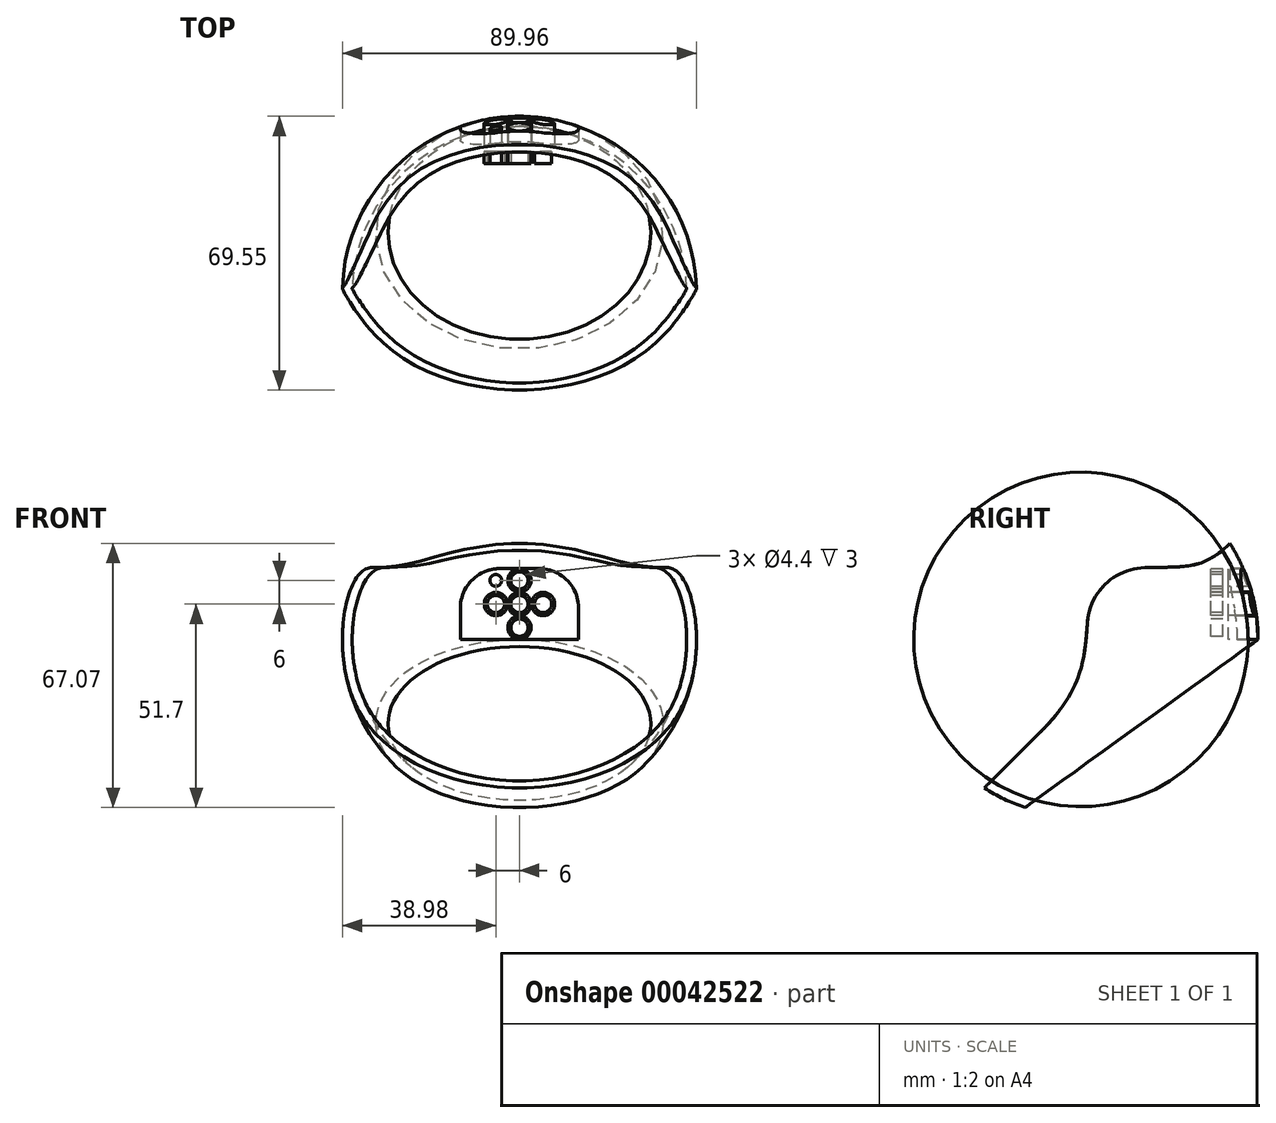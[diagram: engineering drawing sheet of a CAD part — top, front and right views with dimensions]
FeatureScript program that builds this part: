
annotation { "Feature Type Name" : "Feature", "Feature Type Description" : "" }
export const myFeature = defineFeature(function(context is Context, id is Id, definition is map)
    precondition{}
    {
        {
            var Q0;
            Q0=qCreatedBy(makeId("Right.planeOp"),FACE);
            var sketch = newSketch(context, id + "F0", { "sketchPlane" : qUnion([Q0])});
            skArc(sketch, "E0", {"start": v(40, 0) * mm, "mid": v(38.33, 11.42) * mm, "end": v(33.48, 21.9) * mm});
            skLineSegment(sketch, "E1", {"start": v(0, -40) * mm, "end": v(0, 40) * mm, "construction": true});
            skLineSegment(sketch, "E2", {"start": v(-40, 0) * mm, "end": v(40, 0) * mm, "construction": true});
            skPoint(sketch, "E3", {"position": v(33.48, 21.9) * mm});
            skPoint(sketch, "E4", {"position": v(-21.9, -33.48) * mm});
            skLineSegment(sketch, "E5", {"start": v(-21.9, -33.48) * mm, "end": v(33.48, 21.9) * mm, "construction": true});
            skPoint(sketch, "E6", {"position": v(12.26, 0.68) * mm});
            skPoint(sketch, "E7", {"position": v(-7.75, -19.33) * mm});
            skFitSpline(sketch, "E8", {"points": [v(-7.75, -19.33) * mm, v(4.22, 8.7) * mm], "startDerivative": vector(26.03, 26.03) * mm, "endDerivative": vector(-1.06, 47.13) * mm});
            skFitSpline(sketch, "E9", {"points": [v(33.48, 21.9) * mm, v(12.36, 15.68) * mm], "startDerivative": vector(-15.28, -15.28) * mm, "endDerivative": vector(-38.84, 5.85) * mm});
            skArc(sketch, "E10.trimOffspring", {"start": v(20.07, 15.1) * mm, "mid": v(11.15, 14.38) * mm, "end": v(4.22, 8.7) * mm});
            skLineSegment(sketch, "E11", {"start": v(33.48, 21.9) * mm, "end": v(40, 21.9) * mm});
            skLineSegment(sketch, "E12", {"start": v(40, 0) * mm, "end": v(40, 21.9) * mm});
            skCircle(sketch, "E13", {"center": v(0, 0) * mm, "radius": 40 * mm, "construction": true});
            skPoint(sketch, "E14", {"position": v(0, -32.17) * mm});
            skPoint(sketch, "E15", {"position": v(40, 0) * mm});
            skLineSegment(sketch, "E16", {"start": v(-21.9, -33.48) * mm, "end": v(-14.82, -40.55) * mm});
            skLineSegment(sketch, "E17", {"start": v(-14.82, -40.55) * mm, "end": v(40, 0) * mm});
            skLineSegment(sketch, "E18", {"start": v(-14.82, -40.55) * mm, "end": v(-21.9, -40.55) * mm});
            skLineSegment(sketch, "E19", {"start": v(-21.9, -33.48) * mm, "end": v(-21.9, -40.55) * mm});
            skLineSegment(sketch, "E20", {"start": v(-21.9, -33.48) * mm, "end": v(-7.75, -19.33) * mm});
            skPoint(sketch, "E21", {"position": v(-40, 0) * mm});
            skSolve(sketch);
        }
        {
            var Q0;
            Q0=qCreatedBy(makeId("Top.planeOp"),FACE);
            var sketch = newSketch(context, id + "F1", { "sketchPlane" : qUnion([Q0])});
            skArc(sketch, "E22", {"start": v(42.5, 0) * mm, "mid": v(0, 42.5) * mm, "end": v(-42.5, 0) * mm});
            skArc(sketch, "E23", {"start": v(45, 0) * mm, "mid": v(0, 45) * mm, "end": v(-45, 0) * mm});
            skLineSegment(sketch, "E24", {"start": v(16.73, 41.77) * mm, "end": v(7.83, 41.77) * mm});
            skLineSegment(sketch, "E25.trimOffspring", {"start": v(-7.83, 41.77) * mm, "end": v(-16.73, 41.77) * mm});
            skLineSegment(sketch, "E26", {"start": v(45, 0) * mm, "end": v(-45, 0) * mm});
            skSolve(sketch);
        }
        {
            var Q0;
            Q0=qCreatedBy(makeId("Right.planeOp"),FACE);
            cPlane(context, id + "F2", {"entities" : qUnion([Q0]), "cplaneType" : CPlaneType.OFFSET, "offset" : 46.5 * mm, "width" : 150 * mm, "height" : 150 * mm});
        }
        {
            var Q0;
            Q0=qCreatedBy(id+"F2.planeOp",FACE);
            var sketch = newSketch(context, id + "F3", { "sketchPlane" : qUnion([Q0])});
            skPoint(sketch, "E27", {"position": v(-24.55, -37.71) * mm});
            skPoint(sketch, "E28", {"position": v(37.83, 24.37) * mm});
            skPoint(sketch, "E29", {"position": v(45, 0) * mm});
            skPoint(sketch, "E30", {"position": v(-14.2, -42.7) * mm});
            skArc(sketch, "E31", {"start": v(16.18, 18.23) * mm, "mid": v(6.2, 14.04) * mm, "end": v(1.63, 4.22) * mm});
            skFitSpline(sketch, "E32", {"points": [v(-10.49, -23.72) * mm, v(1.63, 4.22) * mm], "startDerivative": vector(31.46, 31.32) * mm, "endDerivative": vector(1.95, 30) * mm});
            skFitSpline(sketch, "E33", {"points": [v(37.83, 24.37) * mm, v(16.18, 18.23) * mm], "startDerivative": vector(-20.08, -19.99) * mm, "endDerivative": vector(-31.5, -0.88) * mm});
            skLineSegment(sketch, "E34.trimOffspring", {"start": v(-10.49, -23.72) * mm, "end": v(-24.55, -37.71) * mm});
            skLineSegment(sketch, "E35", {"start": v(-14.2, -42.7) * mm, "end": v(45, 0) * mm});
            skCircle(sketch, "E36", {"center": v(0, 0) * mm, "radius": 69 * mm});
            skCircle(sketch, "E37", {"center": v(0, 0) * mm, "radius": 45 * mm});
            skLineSegment(sketch, "E38", {"start": v(-14.2, -42.7) * mm, "end": v(-24.55, -42.7) * mm});
            skLineSegment(sketch, "E39", {"start": v(-24.55, -37.71) * mm, "end": v(-24.55, -42.7) * mm});
            skCircle(sketch, "E40", {"center": v(16.6, 3.24) * mm, "radius": 2.2 * mm});
            skCircle(sketch, "E41", {"center": v(16.6, 3.24) * mm, "radius": 3 * mm});
            skSolve(sketch);
        }
        {
            var Q0;
            {var subQ5=sQuery(id+"F1.wireOp",EDGE,"E25.trimOffspring");Q0=makeQuery(id+"F1.imprint","IMPRINT",FACE,{"disambiguationData":[TD([[makeQuery(id+"F1.imprint","IMPRINT",EDGE,{"derivedFrom":subQ5}),1.0]])]});}
            var Q1;
            {var subQ1=sQuery(id+"F1.wireOp",EDGE,"E24");Q1=makeQuery(id+"F1.imprint","IMPRINT",FACE,{"disambiguationData":[TD([[makeQuery(id+"F1.imprint","IMPRINT",EDGE,{"derivedFrom":subQ1}),-1.0]])]});}
            var Q2;
            {var subQ5=sQuery(id+"F1.wireOp",EDGE,"E24");Q2=makeQuery(id+"F1.imprint","IMPRINT",FACE,{"disambiguationData":[TD([[makeQuery(id+"F1.imprint","IMPRINT",EDGE,{"derivedFrom":subQ5}),1.0]])]});}
            var Q3;
            Q3=sQuery(id+"F1.wireOp",EDGE,"E26");
            revolve(context, id + "F4", {"entities" : qUnion([Q0, Q1, Q2]), "axis" : qUnion([Q3]), "revolveType" : RevolveType.TWO_DIRECTIONS, "angle" : 125 * degree, "angleBack" : 280 * degree});
        }
        {
            var Q0;
            Q0=makeQuery(id+"F3.imprint","IMPRINT",FACE,{"disambiguationData":[TD([[makeQuery(id+"F3.imprint","IMPRINT",EDGE,{"derivedFrom":sQuery(id+"F3.wireOp",EDGE,"E31")}),-1.0]])]});
            var Q1;
            {var subQ1=sQuery(id+"F3.wireOp",EDGE,"E35");Q1=makeQuery(id+"F3.imprint","IMPRINT",FACE,{"disambiguationData":[TD([[makeQuery(id+"F3.imprint","IMPRINT",EDGE,{"derivedFrom":subQ1}),-1.0]])]});}
            var Q2;
            Q2=makeQuery(id+"F3.imprint","IMPRINT",FACE,{"disambiguationData":[TD([[makeQuery(id+"F3.imprint","IMPRINT",EDGE,{"derivedFrom":sQuery(id+"F3.wireOp",EDGE,"E36")}),1.0]])]});
            extrude(context, id + "F5", {"entities" : qUnion([Q0, Q1, Q2]), "operationType" : NewBodyOperationType.REMOVE, "endBound" : BoundingType.THROUGH_ALL, "oppositeDirection" : true, "depth" : 25 * mm});
        }
        {
            var Q0;
            Q0=makeQuery(id+"F3.imprint","IMPRINT",FACE,{"disambiguationData":[TD([[makeQuery(id+"F3.imprint","IMPRINT",EDGE,{"derivedFrom":sQuery(id+"F3.wireOp",EDGE,"E31")}),-1.0]])]});
            extrude(context, id + "F6", {"entities" : qUnion([Q0]), "operationType" : NewBodyOperationType.REMOVE, "endBound" : BoundingType.THROUGH_ALL, "depth" : 25 * mm});
        }
        {
            var Q0;
            Q0=qCreatedBy(makeId("Front.planeOp"),FACE);
            cPlane(context, id + "F7", {"entities" : qUnion([Q0]), "cplaneType" : CPlaneType.OFFSET, "offset" : 38 * mm, "oppositeDirection" : true, "width" : 150 * mm, "height" : 150 * mm});
        }
        {
            var Q0;
            Q0=qCreatedBy(id+"F7.planeOp",FACE);
            var sketch = newSketch(context, id + "F8", { "sketchPlane" : qUnion([Q0])});
            skLineSegment(sketch, "E42", {"start": v(0, 0) * mm, "end": v(15, 0) * mm});
            skLineSegment(sketch, "E43", {"start": v(15, 0) * mm, "end": v(15, 18) * mm});
            skLineSegment(sketch, "E44", {"start": v(15, 18) * mm, "end": v(0, 18) * mm});
            skLineSegment(sketch, "E45.MirrorCS", {"start": v(-15, 18) * mm, "end": v(0, 18) * mm});
            skLineSegment(sketch, "E46.MirrorCS", {"start": v(0, 0) * mm, "end": v(-15, 0) * mm});
            skLineSegment(sketch, "E47.MirrorCS", {"start": v(-15, 0) * mm, "end": v(-15, 18) * mm});
            skSolve(sketch);
        }
        {
            var Q0;
            Q0=makeQuery(id+"F8.imprint","IMPRINT",FACE,{"disambiguationData":[TD([[makeQuery(id+"F8.imprint","IMPRINT",EDGE,{"derivedFrom":sQuery(id+"F8.wireOp",EDGE,"E42")}),1.0]])]});
            extrude(context, id + "F9", {"entities" : qUnion([Q0]), "operationType" : NewBodyOperationType.ADD, "depth" : 5 * mm});
        }
        {
            var Q0;
            Q0=makeQuery(id+"F9.opExtrude","CAP_FACE",FACE,{"disambiguationData":[OSD([sQuery(id+"F8.wireOp",EDGE,"E42"),sQuery(id+"F8.wireOp",EDGE,"E43"),sQuery(id+"F8.wireOp",EDGE,"E44"),sQuery(id+"F8.wireOp",EDGE,"E45.MirrorCS"),sQuery(id+"F8.wireOp",EDGE,"E46.MirrorCS"),sQuery(id+"F8.wireOp",EDGE,"E47.MirrorCS")])],"isStart":false});
            var sketch = newSketch(context, id + "F10", { "sketchPlane" : qUnion([Q0])});
            skLineSegment(sketch, "E48", {"start": v(0, 0) * mm, "end": v(0, 18) * mm, "construction": true});
            skLineSegment(sketch, "E49", {"start": v(-15, 9) * mm, "end": v(15, 9) * mm, "construction": true});
            skCircle(sketch, "E50", {"center": v(0, 9) * mm, "radius": 2.95 * mm});
            skCircle(sketch, "E51", {"center": v(-6, 9) * mm, "radius": 2.95 * mm});
            skCircle(sketch, "E52", {"center": v(0, 15) * mm, "radius": 2.95 * mm});
            skCircle(sketch, "E53", {"center": v(0, 15) * mm, "radius": 2.2 * mm});
            skCircle(sketch, "E54", {"center": v(0, 9) * mm, "radius": 2.2 * mm});
            skCircle(sketch, "E55", {"center": v(-6, 9) * mm, "radius": 2.2 * mm});
            skCircle(sketch, "E56.MirrorC", {"center": v(6, 9) * mm, "radius": 2.95 * mm});
            skCircle(sketch, "E57.MirrorC", {"center": v(6, 9) * mm, "radius": 2.2 * mm});
            skCircle(sketch, "E58.MirrorC", {"center": v(0, 3) * mm, "radius": 2.95 * mm});
            skCircle(sketch, "E59.MirrorC", {"center": v(0, 3) * mm, "radius": 2.2 * mm});
            skLineSegment(sketch, "E60", {"start": v(15, 8) * mm, "end": v(15, 9) * mm});
            skLineSegment(sketch, "E61", {"start": v(5, 18) * mm, "end": v(-5, 18) * mm});
            skLineSegment(sketch, "E62", {"start": v(-15, 9) * mm, "end": v(-15, 8) * mm});
            skPoint(sketch, "E63.visualSharp", {"position": v(15, 18) * mm});
            skArc(sketch, "E63.filletArc", {"start": v(15, 8) * mm, "mid": v(12.07, 15.07) * mm, "end": v(5, 18) * mm});
            skPoint(sketch, "E64.visualSharp", {"position": v(-15, 18) * mm});
            skArc(sketch, "E64.filletArc", {"start": v(-5, 18) * mm, "mid": v(-12.07, 15.07) * mm, "end": v(-15, 8) * mm});
            skLineSegment(sketch, "E65", {"start": v(0, 15) * mm, "end": v(9.62, 15) * mm, "construction": true});
            skLineSegment(sketch, "E66", {"start": v(6, 9) * mm, "end": v(6, 16.47) * mm, "construction": true});
            skPoint(sketch, "E67", {"position": v(6, 15) * mm});
            skCircle(sketch, "E68", {"center": v(6, 15) * mm, "radius": 1.5 * mm});
            skCircle(sketch, "E69.MirrorC", {"center": v(-6, 15) * mm, "radius": 1.5 * mm});
            skSolve(sketch);
        }
        {
            var Q0;
            Q0=makeQuery(id+"F9.opExtrude","SWEPT_FACE",FACE,{"disambiguationData":[OSD([sQuery(id+"F8.wireOp",EDGE,"E42"),sQuery(id+"F8.wireOp",EDGE,"E46.MirrorCS")])]});
            var sketch = newSketch(context, id + "F11", { "sketchPlane" : qUnion([Q0])});
            skLineSegment(sketch, "E70", {"start": v(0, -38) * mm, "end": v(0, -33) * mm, "construction": true});
            skPoint(sketch, "E71", {"position": v(-12, -33) * mm});
            skPoint(sketch, "E72", {"position": v(0, -36) * mm});
            skPoint(sketch, "E73", {"position": v(0, -37.5) * mm});
            skLineSegment(sketch, "E74", {"start": v(-12, -36) * mm, "end": v(-12, -37.5) * mm});
            skLineSegment(sketch, "E75", {"start": v(0, -37.5) * mm, "end": v(-12, -37.5) * mm});
            skLineSegment(sketch, "E76", {"start": v(0, -36) * mm, "end": v(-12, -36) * mm});
            skLineSegment(sketch, "E77.MirrorCS", {"start": v(0, -36) * mm, "end": v(12, -36) * mm});
            skLineSegment(sketch, "E78.MirrorCS", {"start": v(12, -36) * mm, "end": v(12, -37.5) * mm});
            skLineSegment(sketch, "E79.MirrorCS", {"start": v(0, -37.5) * mm, "end": v(12, -37.5) * mm});
            skSolve(sketch);
        }
        {
            var Q0;
            Q0=makeQuery(id+"F11.imprint","IMPRINT",FACE,{"disambiguationData":[TD([[makeQuery(id+"F11.imprint","IMPRINT",EDGE,{"derivedFrom":sQuery(id+"F11.wireOp",EDGE,"E74")}),1.0]])]});
            var Q1;
            Q1=makeQuery(id+"F4.opRevolve","SWEPT_FACE",FACE,{"disambiguationData":[OSD([sQuery(id+"F1.wireOp",EDGE,"E22")])]});
            var Q2;
            Q2=makeQuery(id+"F4.opRevolve","SWEPT_BODY",BODY,{"disambiguationData":[OSD([sQuery(id+"F1.wireOp",EDGE,"E22"),sQuery(id+"F1.wireOp",EDGE,"E23"),sQuery(id+"F1.wireOp",EDGE,"E26")])]});
            extrude(context, id + "F12", {"entities" : qUnion([Q0]), "operationType" : NewBodyOperationType.REMOVE, "endBound" : BoundingType.UP_TO_SURFACE, "oppositeDirection" : true, "endBoundEntityFace" : qUnion([Q1]), "endBoundEntityBody" : qUnion([Q2]), "depth" : 25 * mm});
        }
        {
            var Q0;
            Q0=makeQuery(id+"F10.imprint","IMPRINT",FACE,{"disambiguationData":[TD([[makeQuery(id+"F10.imprint","IMPRINT",EDGE,{"derivedFrom":sQuery(id+"F10.wireOp",EDGE,"E55")}),1.0]])]});
            var Q1;
            Q1=makeQuery(id+"F10.imprint","IMPRINT",FACE,{"disambiguationData":[TD([[makeQuery(id+"F10.imprint","IMPRINT",EDGE,{"derivedFrom":sQuery(id+"F10.wireOp",EDGE,"E53")}),1.0]])]});
            var Q2;
            Q2=makeQuery(id+"F10.imprint","IMPRINT",FACE,{"disambiguationData":[TD([[makeQuery(id+"F10.imprint","IMPRINT",EDGE,{"derivedFrom":sQuery(id+"F10.wireOp",EDGE,"E59.MirrorC")}),-1.0]])]});
            var Q3;
            Q3=makeQuery(id+"F10.imprint","IMPRINT",FACE,{"disambiguationData":[TD([[makeQuery(id+"F10.imprint","IMPRINT",EDGE,{"derivedFrom":sQuery(id+"F10.wireOp",EDGE,"E57.MirrorC")}),-1.0]])]});
            var Q4;
            Q4=makeQuery(id+"F10.imprint","IMPRINT",FACE,{"disambiguationData":[TD([[makeQuery(id+"F10.imprint","IMPRINT",EDGE,{"derivedFrom":sQuery(id+"F10.wireOp",EDGE,"E54")}),1.0]])]});
            extrude(context, id + "F13", {"entities" : qUnion([Q0, Q1, Q2, Q3, Q4]), "operationType" : NewBodyOperationType.REMOVE, "endBound" : BoundingType.UP_TO_NEXT, "oppositeDirection" : true, "depth" : 25 * mm});
        }
        {
            var Q0;
            {var subQ1=sQuery(id+"F10.wireOp",EDGE,"E64.filletArc");Q0=makeQuery(id+"F10.imprint","IMPRINT",FACE,{"disambiguationData":[TD([[makeQuery(id+"F10.imprint","IMPRINT",EDGE,{"derivedFrom":subQ1}),-1.0]])]});}
            var Q1;
            {var subQ1=sQuery(id+"F10.wireOp",EDGE,"E63.filletArc");Q1=makeQuery(id+"F10.imprint","IMPRINT",FACE,{"disambiguationData":[TD([[makeQuery(id+"F10.imprint","IMPRINT",EDGE,{"derivedFrom":subQ1}),-1.0]])]});}
            var Q2;
            {var subQ0=sQuery(id+"F1.wireOp",EDGE,"E22");Q2=makeQuery(id+"F12.boolean.opBoolean","MERGE",FACE,{"derivedFrom":[makeQuery(id+"F4.opRevolve","SWEPT_FACE",FACE,{"disambiguationData":[OSD([subQ0])]}),makeQuery(id+"F12.opExtrude","CAP_FACE",FACE,{"disambiguationData":[OSD([subQ0])],"isStart":false})]});}
            extrude(context, id + "F14", {"entities" : qUnion([Q0, Q1]), "operationType" : NewBodyOperationType.REMOVE, "endBound" : BoundingType.UP_TO_SURFACE, "oppositeDirection" : true, "endBoundEntityFace" : qUnion([Q2]), "depth" : 25 * mm});
        }
        {
            var Q0;
            Q0=makeQuery(id+"F9.opExtrude","CAP_FACE",FACE,{"disambiguationData":[OSD([sQuery(id+"F8.wireOp",EDGE,"E42"),sQuery(id+"F8.wireOp",EDGE,"E43"),sQuery(id+"F8.wireOp",EDGE,"E44"),sQuery(id+"F8.wireOp",EDGE,"E45.MirrorCS"),sQuery(id+"F8.wireOp",EDGE,"E46.MirrorCS"),sQuery(id+"F8.wireOp",EDGE,"E47.MirrorCS")])],"isStart":true});
            extrude(context, id + "F15", {"entities" : qUnion([Q0]), "operationType" : NewBodyOperationType.ADD, "endBound" : BoundingType.UP_TO_NEXT, "depth" : 25 * mm});
        }
        {
            var Q0;
            Q0=makeQuery(id+"F10.imprint","IMPRINT",FACE,{"disambiguationData":[TD([[makeQuery(id+"F10.imprint","IMPRINT",EDGE,{"derivedFrom":sQuery(id+"F10.wireOp",EDGE,"E69.MirrorC")}),-1.0]])]});
            var Q1;
            Q1=makeQuery(id+"F10.imprint","IMPRINT",FACE,{"disambiguationData":[TD([[makeQuery(id+"F10.imprint","IMPRINT",EDGE,{"derivedFrom":sQuery(id+"F10.wireOp",EDGE,"E68")}),1.0]])]});
            extrude(context, id + "F16", {"entities" : qUnion([Q0, Q1]), "operationType" : NewBodyOperationType.REMOVE, "endBound" : BoundingType.THROUGH_ALL, "oppositeDirection" : true, "depth" : 25 * mm});
        }
    });
